# Revit family: L-EP-933-DN_RFA
name_source: partatom
category: Aparatos sanitarios
units: mm (PartAtom-declared; Revit-internal decimal feet)

## family parameters
Activar corte en vistas = No
Compartido = Sí
Corte con vacíos al cargar = No
Cota de conector redondo = Usar diámetro
Mantener orientación de anotación = No
Número OmniClass = 23.45.55.14
Punto de cálculo de habitación = Sí
Se basa en plano de trabajo = Sí
Siempre vertical = Sí
Tipo de pieza = Normal
Título OmniClass = Single Faucets

## types (1)
- L-EP-933-TN
    Características del Producto = Monomando para lavabo alto limited, incluye
contra de push.
Cartucho monomando de 35 mm con vástago
metálico.
Discos cerámicos de alta dureza que extienden
y aseguran la vida del cartucho sin fugas.
Fácil instalación y mantenimiento.
    Componentes Incluidos = Llave hexagonal para la instalación.
Llave para mantenimiento.
Llave allen 5/64"
Contra de push con rebosadero.
Inserto para usarse con lavabos sin rebosadero.
    Cuerpo de Latón = Brass
    Descripción = Monomando para Lavabo Alto Limited, Incluye Contra de Push
    Elevación por defecto = 1"
    Fabricante = HELVEX S.A. de C.V.
    Garantía = El producto HELVEX está garantizado como
libre de defectos en materiales, mano de obra y
procesos de fabricación.
El producto HELVEX está garantizado,en lo que
se refiere a los acabados, por 10 años para los
acabados Cromo y Duravex, y por 2 años en
acabados diferentes al Cromo y Duravex.
Las piezas que sufren desgaste natural en el
producto están garantizadas para uso
residencial por 5 años, y para uso comercial por
3 años.
La vigencia de la garantía inicia a partir de la
fecha de entrega del producto al consumidor
indicada en la Póliza de Garantía.
    Imagen de tipo = <Ninguno>
    Instalación = Conexión ½ - 14 NPSM
    Modelo = L-EP-933-TN
    Operación = Para abrir el flujo de agua levante la palanca y
para cerrar baje la palanca.
Para el agua caliente gire el maneral hacia la
izquierda y para el agua fría gire hacia la
derecha.
    Presión Máxima de Trabajo = 85.3 psi
    Presión Mínima de Trabajo = 3.5 psi
    Total Depth = 7"
    Total Height = 12"
    Total Width = 2"

## geometry (parser evidence)
native form markers: Sweep x3
no freeform markers — native parametric forms only
